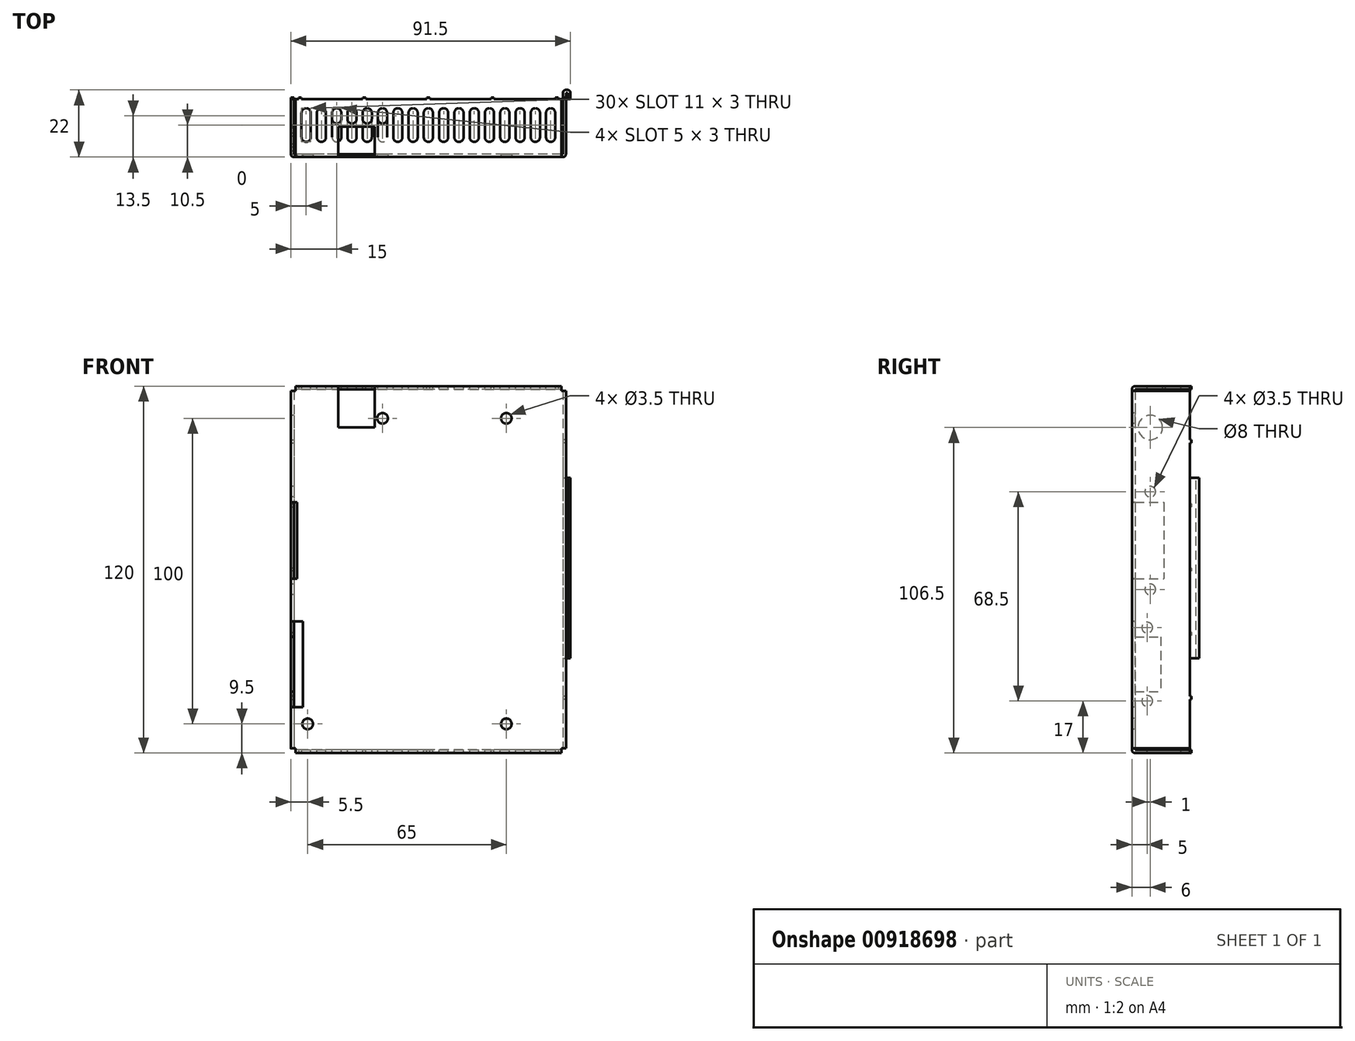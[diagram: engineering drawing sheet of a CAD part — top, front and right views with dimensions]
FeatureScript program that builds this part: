
annotation { "Feature Type Name" : "Feature", "Feature Type Description" : "" }
export const myFeature = defineFeature(function(context is Context, id is Id, definition is map)
    precondition{}
    {
        {
            var Q0;
            Q0=qCreatedBy(makeId("Front.planeOp"),FACE);
            var sketch = newSketch(context, id + "F0", { "sketchPlane" : qUnion([Q0])});
            skLineSegment(sketch, "E0.bottom", {"start": v(-45, 60) * mm, "end": v(45, 60) * mm});
            skLineSegment(sketch, "E0.top", {"start": v(-45, -60) * mm, "end": v(45, -60) * mm});
            skLineSegment(sketch, "E0.left", {"start": v(-45, 60) * mm, "end": v(-45, -60) * mm});
            skLineSegment(sketch, "E0.right", {"start": v(45, 60) * mm, "end": v(45, -60) * mm});
            skPoint(sketch, "E1", {"position": v(45, 0) * mm});
            skPoint(sketch, "E2", {"position": v(0, 60) * mm});
            skSolve(sketch);
        }
        {
            var Q0;
            Q0=qSketchRegion(id+"F0",true);
            extrude(context, id + "F1", {"entities" : qUnion([Q0]), "oppositeDirection" : true, "depth" : 1 * mm, "offsetDistance" : 25 * mm});
        }
        {
            var Q0;
            Q0=makeQuery(id+"F1.opExtrude","CAP_FACE",FACE,{"disambiguationData":[OSD([sQuery(id+"F0.wireOp",EDGE,"E0.bottom"),sQuery(id+"F0.wireOp",EDGE,"E0.top"),sQuery(id+"F0.wireOp",EDGE,"E0.left"),sQuery(id+"F0.wireOp",EDGE,"E0.right")])],"isStart":false});
            var sketch = newSketch(context, id + "F2", { "sketchPlane" : qUnion([Q0])});
            skLineSegment(sketch, "E3.bottom", {"start": v(-43.5, 60) * mm, "end": v(43.5, 60) * mm});
            skLineSegment(sketch, "E3.top", {"start": v(-43.5, 59) * mm, "end": v(43.5, 59) * mm});
            skLineSegment(sketch, "E3.left", {"start": v(-43.5, 60) * mm, "end": v(-43.5, 59) * mm});
            skLineSegment(sketch, "E3.right", {"start": v(43.5, 60) * mm, "end": v(43.5, 59) * mm});
            skLineSegment(sketch, "E4.bottom", {"start": v(-45, 58.5) * mm, "end": v(-44, 58.5) * mm});
            skLineSegment(sketch, "E4.top", {"start": v(-45, -58.5) * mm, "end": v(-44, -58.5) * mm});
            skLineSegment(sketch, "E4.left", {"start": v(-45, 58.5) * mm, "end": v(-45, -58.5) * mm});
            skLineSegment(sketch, "E4.right", {"start": v(-44, 58.5) * mm, "end": v(-44, -58.5) * mm});
            skLineSegment(sketch, "E5.bottom", {"start": v(45, 58.5) * mm, "end": v(44, 58.5) * mm});
            skLineSegment(sketch, "E5.top", {"start": v(45, -58.5) * mm, "end": v(44, -58.5) * mm});
            skLineSegment(sketch, "E5.left", {"start": v(45, 58.5) * mm, "end": v(45, -58.5) * mm});
            skLineSegment(sketch, "E5.right", {"start": v(44, 58.5) * mm, "end": v(44, -58.5) * mm});
            skLineSegment(sketch, "E6.bottom", {"start": v(-43.5, -59) * mm, "end": v(43.5, -59) * mm});
            skLineSegment(sketch, "E6.top", {"start": v(-43.5, -60) * mm, "end": v(43.5, -60) * mm});
            skLineSegment(sketch, "E6.left", {"start": v(-43.5, -59) * mm, "end": v(-43.5, -60) * mm});
            skLineSegment(sketch, "E6.right", {"start": v(43.5, -59) * mm, "end": v(43.5, -60) * mm});
            skSolve(sketch);
        }
        {
            var Q0;
            Q0=qSketchRegion(id+"F2",true);
            extrude(context, id + "F3", {"entities" : qUnion([Q0]), "operationType" : NewBodyOperationType.ADD, "depth" : 18 * mm, "offsetDistance" : 25 * mm});
        }
        {
            var Q0;
            Q0=makeQuery(id+"F1.opExtrude","CAP_FACE",FACE,{"disambiguationData":[OSD([sQuery(id+"F0.wireOp",EDGE,"E0.bottom"),sQuery(id+"F0.wireOp",EDGE,"E0.top"),sQuery(id+"F0.wireOp",EDGE,"E0.left"),sQuery(id+"F0.wireOp",EDGE,"E0.right")])],"isStart":false});
            var sketch = newSketch(context, id + "F4", { "sketchPlane" : qUnion([Q0])});
            skLineSegment(sketch, "E7.bottom", {"start": v(43.5, 60) * mm, "end": v(45, 60) * mm});
            skLineSegment(sketch, "E7.top", {"start": v(43.5, 58.5) * mm, "end": v(45, 58.5) * mm});
            skLineSegment(sketch, "E7.left", {"start": v(43.5, 60) * mm, "end": v(43.5, 58.5) * mm});
            skLineSegment(sketch, "E7.right", {"start": v(45, 60) * mm, "end": v(45, 58.5) * mm});
            skLineSegment(sketch, "E8.bottom", {"start": v(-45, 58.5) * mm, "end": v(-43.5, 58.5) * mm});
            skLineSegment(sketch, "E8.top", {"start": v(-45, 60) * mm, "end": v(-43.5, 60) * mm});
            skLineSegment(sketch, "E8.left", {"start": v(-45, 58.5) * mm, "end": v(-45, 60) * mm});
            skLineSegment(sketch, "E8.right", {"start": v(-43.5, 58.5) * mm, "end": v(-43.5, 60) * mm});
            skLineSegment(sketch, "E9.bottom", {"start": v(43.5, -60) * mm, "end": v(45, -60) * mm});
            skLineSegment(sketch, "E9.top", {"start": v(43.5, -58.5) * mm, "end": v(45, -58.5) * mm});
            skLineSegment(sketch, "E9.left", {"start": v(43.5, -60) * mm, "end": v(43.5, -58.5) * mm});
            skLineSegment(sketch, "E9.right", {"start": v(45, -60) * mm, "end": v(45, -58.5) * mm});
            skLineSegment(sketch, "E10.bottom", {"start": v(-45, -58.5) * mm, "end": v(-43.5, -58.5) * mm});
            skLineSegment(sketch, "E10.top", {"start": v(-45, -60) * mm, "end": v(-43.5, -60) * mm});
            skLineSegment(sketch, "E10.left", {"start": v(-45, -58.5) * mm, "end": v(-45, -60) * mm});
            skLineSegment(sketch, "E10.right", {"start": v(-43.5, -58.5) * mm, "end": v(-43.5, -60) * mm});
            skSolve(sketch);
        }
        {
            var Q0;
            Q0=qSketchRegion(id+"F4",true);
            extrude(context, id + "F5", {"entities" : qUnion([Q0]), "operationType" : NewBodyOperationType.REMOVE, "endBound" : BoundingType.THROUGH_ALL, "oppositeDirection" : true, "depth" : 25 * mm, "offsetDistance" : 25 * mm});
        }
        {
            var Q0;
            Q0=makeQuery(id+"F3.boolean.opBoolean","MERGE",FACE,{"derivedFrom":[makeQuery(id+"F1.opExtrude","SWEPT_FACE",FACE,{"disambiguationData":[OSD([sQuery(id+"F0.wireOp",EDGE,"E0.bottom")])]}),makeQuery(id+"F3.opExtrude","SWEPT_FACE",FACE,{"disambiguationData":[OSD([sQuery(id+"F2.wireOp",EDGE,"E3.bottom")])]})]});
            var sketch = newSketch(context, id + "F6", { "sketchPlane" : qUnion([Q0])});
            skLineSegment(sketch, "E11.left", {"start": v(1.5, 6.5) * mm, "end": v(1.5, 14.5) * mm});
            skLineSegment(sketch, "E11.right", {"start": v(-1.5, 6.5) * mm, "end": v(-1.5, 14.5) * mm});
            skArc(sketch, "E12", {"start": v(-1.5, 6.5) * mm, "mid": v(0, 5) * mm, "end": v(1.5, 6.5) * mm});
            skArc(sketch, "E13", {"start": v(1.5, 14.5) * mm, "mid": v(0, 16) * mm, "end": v(-1.5, 14.5) * mm});
            skPoint(sketch, "E14", {"position": v(0, 5) * mm});
            skPoint(sketch, "E15", {"position": v(0, 16) * mm});
            skLineSegment(sketch, "E16.left", {"start": v(-3.5, 6.5) * mm, "end": v(-3.5, 14.5) * mm});
            skLineSegment(sketch, "E16.right", {"start": v(-6.5, 6.5) * mm, "end": v(-6.5, 14.5) * mm});
            skArc(sketch, "E17", {"start": v(-6.5, 6.5) * mm, "mid": v(-5, 5) * mm, "end": v(-3.5, 6.5) * mm});
            skArc(sketch, "E18", {"start": v(-3.5, 14.5) * mm, "mid": v(-5, 16) * mm, "end": v(-6.5, 14.5) * mm});
            skPoint(sketch, "E19", {"position": v(-5, 5) * mm});
            skPoint(sketch, "E20", {"position": v(-5, 16) * mm});
            skLineSegment(sketch, "E21.left", {"start": v(-8.5, 6.5) * mm, "end": v(-8.5, 14.5) * mm});
            skLineSegment(sketch, "E21.right", {"start": v(-11.5, 6.5) * mm, "end": v(-11.5, 14.5) * mm});
            skArc(sketch, "E22", {"start": v(-11.5, 6.5) * mm, "mid": v(-10, 5) * mm, "end": v(-8.5, 6.5) * mm});
            skArc(sketch, "E23", {"start": v(-8.5, 14.5) * mm, "mid": v(-10, 16) * mm, "end": v(-11.5, 14.5) * mm});
            skPoint(sketch, "E24", {"position": v(-10, 5) * mm});
            skPoint(sketch, "E25", {"position": v(-10, 16) * mm});
            skLineSegment(sketch, "E26.left", {"start": v(-13.5, 12.5) * mm, "end": v(-13.5, 14.5) * mm});
            skLineSegment(sketch, "E26.right", {"start": v(-16.5, 12.5) * mm, "end": v(-16.5, 14.5) * mm});
            skArc(sketch, "E27", {"start": v(-16.5, 12.5) * mm, "mid": v(-15, 11) * mm, "end": v(-13.5, 12.5) * mm});
            skArc(sketch, "E28", {"start": v(-13.5, 14.5) * mm, "mid": v(-15, 16) * mm, "end": v(-16.5, 14.5) * mm});
            skPoint(sketch, "E29", {"position": v(-15, 11) * mm});
            skPoint(sketch, "E30", {"position": v(-15, 16) * mm});
            skLineSegment(sketch, "E31.left", {"start": v(11.5, 6.5) * mm, "end": v(11.5, 14.5) * mm});
            skLineSegment(sketch, "E31.right", {"start": v(8.5, 6.5) * mm, "end": v(8.5, 14.5) * mm});
            skArc(sketch, "E32", {"start": v(8.5, 6.5) * mm, "mid": v(10, 5) * mm, "end": v(11.5, 6.5) * mm});
            skArc(sketch, "E33", {"start": v(11.5, 14.5) * mm, "mid": v(10, 16) * mm, "end": v(8.5, 14.5) * mm});
            skPoint(sketch, "E34", {"position": v(10, 5) * mm});
            skPoint(sketch, "E35", {"position": v(10, 16) * mm});
            skLineSegment(sketch, "E36.left", {"start": v(6.5, 6.5) * mm, "end": v(6.5, 14.5) * mm});
            skLineSegment(sketch, "E36.right", {"start": v(3.5, 6.5) * mm, "end": v(3.5, 14.5) * mm});
            skArc(sketch, "E37", {"start": v(3.5, 6.5) * mm, "mid": v(5, 5) * mm, "end": v(6.5, 6.5) * mm});
            skArc(sketch, "E38", {"start": v(6.5, 14.5) * mm, "mid": v(5, 16) * mm, "end": v(3.5, 14.5) * mm});
            skPoint(sketch, "E39", {"position": v(5, 5) * mm});
            skPoint(sketch, "E40", {"position": v(5, 16) * mm});
            skLineSegment(sketch, "E41.left", {"start": v(16.5, 6.5) * mm, "end": v(16.5, 14.5) * mm});
            skLineSegment(sketch, "E41.right", {"start": v(13.5, 6.5) * mm, "end": v(13.5, 14.5) * mm});
            skArc(sketch, "E42", {"start": v(13.5, 6.5) * mm, "mid": v(15, 5) * mm, "end": v(16.5, 6.5) * mm});
            skArc(sketch, "E43", {"start": v(16.5, 14.5) * mm, "mid": v(15, 16) * mm, "end": v(13.5, 14.5) * mm});
            skPoint(sketch, "E44", {"position": v(15, 5) * mm});
            skPoint(sketch, "E45", {"position": v(15, 16) * mm});
            skLineSegment(sketch, "E46.left", {"start": v(-18.5, 12.5) * mm, "end": v(-18.5, 14.5) * mm});
            skLineSegment(sketch, "E46.right", {"start": v(-21.5, 12.5) * mm, "end": v(-21.5, 14.5) * mm});
            skArc(sketch, "E47", {"start": v(-21.5, 12.5) * mm, "mid": v(-20, 11) * mm, "end": v(-18.5, 12.5) * mm});
            skArc(sketch, "E48", {"start": v(-18.5, 14.5) * mm, "mid": v(-20, 16) * mm, "end": v(-21.5, 14.5) * mm});
            skPoint(sketch, "E49", {"position": v(-20, 11) * mm});
            skPoint(sketch, "E50", {"position": v(-20, 16) * mm});
            skLineSegment(sketch, "E51.left", {"start": v(-23.5, 12.5) * mm, "end": v(-23.5, 14.5) * mm});
            skLineSegment(sketch, "E51.right", {"start": v(-26.5, 12.5) * mm, "end": v(-26.5, 14.5) * mm});
            skArc(sketch, "E52", {"start": v(-26.5, 12.5) * mm, "mid": v(-25, 11) * mm, "end": v(-23.5, 12.5) * mm});
            skArc(sketch, "E53", {"start": v(-23.5, 14.5) * mm, "mid": v(-25, 16) * mm, "end": v(-26.5, 14.5) * mm});
            skPoint(sketch, "E54", {"position": v(-25, 5) * mm});
            skPoint(sketch, "E55", {"position": v(-25, 16) * mm});
            skLineSegment(sketch, "E56.left", {"start": v(-28.5, 12.5) * mm, "end": v(-28.5, 14.5) * mm});
            skLineSegment(sketch, "E56.right", {"start": v(-31.5, 12.5) * mm, "end": v(-31.5, 14.5) * mm});
            skArc(sketch, "E57", {"start": v(-31.5, 12.5) * mm, "mid": v(-30, 11) * mm, "end": v(-28.5, 12.5) * mm});
            skArc(sketch, "E58", {"start": v(-28.5, 14.5) * mm, "mid": v(-30, 16) * mm, "end": v(-31.5, 14.5) * mm});
            skPoint(sketch, "E59", {"position": v(-30, 11) * mm});
            skPoint(sketch, "E60", {"position": v(-30, 16) * mm});
            skLineSegment(sketch, "E61.left", {"start": v(-33.5, 6.5) * mm, "end": v(-33.5, 14.5) * mm});
            skLineSegment(sketch, "E61.right", {"start": v(-36.5, 6.5) * mm, "end": v(-36.5, 14.5) * mm});
            skArc(sketch, "E62", {"start": v(-36.5, 6.5) * mm, "mid": v(-35, 5) * mm, "end": v(-33.5, 6.5) * mm});
            skArc(sketch, "E63", {"start": v(-33.5, 14.5) * mm, "mid": v(-35, 16) * mm, "end": v(-36.5, 14.5) * mm});
            skPoint(sketch, "E64", {"position": v(-35, 5) * mm});
            skPoint(sketch, "E65", {"position": v(-35, 16) * mm});
            skLineSegment(sketch, "E66.left", {"start": v(36.5, 6.5) * mm, "end": v(36.5, 14.5) * mm});
            skLineSegment(sketch, "E66.right", {"start": v(33.5, 6.5) * mm, "end": v(33.5, 14.5) * mm});
            skArc(sketch, "E67", {"start": v(33.5, 6.5) * mm, "mid": v(35, 5) * mm, "end": v(36.5, 6.5) * mm});
            skArc(sketch, "E68", {"start": v(36.5, 14.5) * mm, "mid": v(35, 16) * mm, "end": v(33.5, 14.5) * mm});
            skPoint(sketch, "E69", {"position": v(35, 5) * mm});
            skPoint(sketch, "E70", {"position": v(35, 16) * mm});
            skLineSegment(sketch, "E71.left", {"start": v(31.5, 6.5) * mm, "end": v(31.5, 14.5) * mm});
            skLineSegment(sketch, "E71.right", {"start": v(28.5, 6.5) * mm, "end": v(28.5, 14.5) * mm});
            skArc(sketch, "E72", {"start": v(28.5, 6.5) * mm, "mid": v(30, 5) * mm, "end": v(31.5, 6.5) * mm});
            skArc(sketch, "E73", {"start": v(31.5, 14.5) * mm, "mid": v(30, 16) * mm, "end": v(28.5, 14.5) * mm});
            skPoint(sketch, "E74", {"position": v(30, 5) * mm});
            skPoint(sketch, "E75", {"position": v(30, 16) * mm});
            skLineSegment(sketch, "E76.left", {"start": v(26.5, 6.5) * mm, "end": v(26.5, 14.5) * mm});
            skLineSegment(sketch, "E76.right", {"start": v(23.5, 6.5) * mm, "end": v(23.5, 14.5) * mm});
            skArc(sketch, "E77", {"start": v(23.5, 6.5) * mm, "mid": v(25, 5) * mm, "end": v(26.5, 6.5) * mm});
            skArc(sketch, "E78", {"start": v(26.5, 14.5) * mm, "mid": v(25, 16) * mm, "end": v(23.5, 14.5) * mm});
            skPoint(sketch, "E79", {"position": v(25, 5) * mm});
            skPoint(sketch, "E80", {"position": v(25, 16) * mm});
            skLineSegment(sketch, "E81.left", {"start": v(21.5, 6.5) * mm, "end": v(21.5, 14.5) * mm});
            skLineSegment(sketch, "E81.right", {"start": v(18.5, 6.5) * mm, "end": v(18.5, 14.5) * mm});
            skArc(sketch, "E82", {"start": v(18.5, 6.5) * mm, "mid": v(20, 5) * mm, "end": v(21.5, 6.5) * mm});
            skArc(sketch, "E83", {"start": v(21.5, 14.5) * mm, "mid": v(20, 16) * mm, "end": v(18.5, 14.5) * mm});
            skPoint(sketch, "E84", {"position": v(20, 5) * mm});
            skPoint(sketch, "E85", {"position": v(20, 16) * mm});
            skLineSegment(sketch, "E86.left", {"start": v(-38.5, 6.5) * mm, "end": v(-38.5, 14.5) * mm});
            skLineSegment(sketch, "E86.right", {"start": v(-41.5, 6.5) * mm, "end": v(-41.5, 14.5) * mm});
            skArc(sketch, "E87", {"start": v(-41.5, 6.5) * mm, "mid": v(-40, 5) * mm, "end": v(-38.5, 6.5) * mm});
            skArc(sketch, "E88", {"start": v(-38.5, 14.5) * mm, "mid": v(-40, 16) * mm, "end": v(-41.5, 14.5) * mm});
            skPoint(sketch, "E89", {"position": v(-40, 5) * mm});
            skPoint(sketch, "E90", {"position": v(-40, 16) * mm});
            skLineSegment(sketch, "E91.left", {"start": v(41.5, 6.5) * mm, "end": v(41.5, 14.5) * mm});
            skLineSegment(sketch, "E91.right", {"start": v(38.5, 6.5) * mm, "end": v(38.5, 14.5) * mm});
            skArc(sketch, "E92", {"start": v(38.5, 6.5) * mm, "mid": v(40, 5) * mm, "end": v(41.5, 6.5) * mm});
            skArc(sketch, "E93", {"start": v(41.5, 14.5) * mm, "mid": v(40, 16) * mm, "end": v(38.5, 14.5) * mm});
            skPoint(sketch, "E94", {"position": v(40, 5) * mm});
            skPoint(sketch, "E95", {"position": v(40, 16) * mm});
            skSolve(sketch);
        }
        {
            var Q0;
            Q0=qSketchRegion(id+"F6",true);
            extrude(context, id + "F7", {"entities" : qUnion([Q0]), "operationType" : NewBodyOperationType.REMOVE, "endBound" : BoundingType.THROUGH_ALL, "oppositeDirection" : true, "depth" : 25 * mm, "offsetDistance" : 25 * mm});
        }
        {
            var Q0;
            Q0=makeQuery(id+"F3.opExtrude","CAP_FACE",FACE,{"disambiguationData":[OSD([sQuery(id+"F2.wireOp",EDGE,"E5.bottom"),sQuery(id+"F2.wireOp",EDGE,"E5.top"),sQuery(id+"F2.wireOp",EDGE,"E5.left"),sQuery(id+"F2.wireOp",EDGE,"E5.right")])],"isStart":false});
            var sketch = newSketch(context, id + "F8", { "sketchPlane" : qUnion([Q0])});
            skLineSegment(sketch, "E96.bottom", {"start": v(0.5, -60) * mm, "end": v(-0.5, -60) * mm});
            skLineSegment(sketch, "E96.top", {"start": v(0.5, -59) * mm, "end": v(-0.5, -59) * mm});
            skLineSegment(sketch, "E96.left", {"start": v(0.5, -60) * mm, "end": v(0.5, -59) * mm});
            skLineSegment(sketch, "E96.right", {"start": v(-0.5, -60) * mm, "end": v(-0.5, -59) * mm});
            skLineSegment(sketch, "E97.bottom", {"start": v(0.5, 59) * mm, "end": v(-0.5, 59) * mm});
            skLineSegment(sketch, "E97.top", {"start": v(0.5, 60) * mm, "end": v(-0.5, 60) * mm});
            skLineSegment(sketch, "E97.left", {"start": v(0.5, 59) * mm, "end": v(0.5, 60) * mm});
            skLineSegment(sketch, "E97.right", {"start": v(-0.5, 59) * mm, "end": v(-0.5, 60) * mm});
            skLineSegment(sketch, "E98.bottom", {"start": v(45, 20.5) * mm, "end": v(44, 20.5) * mm});
            skLineSegment(sketch, "E98.top", {"start": v(45, 21.5) * mm, "end": v(44, 21.5) * mm});
            skLineSegment(sketch, "E98.left", {"start": v(45, 20.5) * mm, "end": v(45, 21.5) * mm});
            skLineSegment(sketch, "E98.right", {"start": v(44, 20.5) * mm, "end": v(44, 21.5) * mm});
            skLineSegment(sketch, "E99.bottom", {"start": v(45, -21.5) * mm, "end": v(44, -21.5) * mm});
            skLineSegment(sketch, "E99.top", {"start": v(45, -20.5) * mm, "end": v(44, -20.5) * mm});
            skLineSegment(sketch, "E99.left", {"start": v(45, -21.5) * mm, "end": v(45, -20.5) * mm});
            skLineSegment(sketch, "E99.right", {"start": v(44, -21.5) * mm, "end": v(44, -20.5) * mm});
            skPoint(sketch, "E100", {"position": v(0, -59) * mm});
            skPoint(sketch, "E101", {"position": v(0, 59) * mm});
            skPoint(sketch, "E102", {"position": v(44, 21) * mm});
            skPoint(sketch, "E103", {"position": v(44, -21) * mm});
            skLineSegment(sketch, "E104.bottom", {"start": v(44, 0.5) * mm, "end": v(45, 0.5) * mm});
            skLineSegment(sketch, "E104.top", {"start": v(44, -0.5) * mm, "end": v(45, -0.5) * mm});
            skLineSegment(sketch, "E104.left", {"start": v(44, 0.5) * mm, "end": v(44, -0.5) * mm});
            skLineSegment(sketch, "E104.right", {"start": v(45, 0.5) * mm, "end": v(45, -0.5) * mm});
            skPoint(sketch, "E105", {"position": v(44, 0) * mm});
            skLineSegment(sketch, "E106.bottom", {"start": v(45, -42.5) * mm, "end": v(44, -42.5) * mm});
            skLineSegment(sketch, "E106.top", {"start": v(45, -41.5) * mm, "end": v(44, -41.5) * mm});
            skLineSegment(sketch, "E106.left", {"start": v(45, -42.5) * mm, "end": v(45, -41.5) * mm});
            skLineSegment(sketch, "E106.right", {"start": v(44, -42.5) * mm, "end": v(44, -41.5) * mm});
            skPoint(sketch, "E107", {"position": v(45, -42) * mm});
            skLineSegment(sketch, "E108.bottom", {"start": v(21.5, -60) * mm, "end": v(20.5, -60) * mm});
            skLineSegment(sketch, "E108.top", {"start": v(21.5, -59) * mm, "end": v(20.5, -59) * mm});
            skLineSegment(sketch, "E108.left", {"start": v(20.5, -60) * mm, "end": v(20.5, -59) * mm});
            skLineSegment(sketch, "E108.right", {"start": v(21.5, -60) * mm, "end": v(21.5, -59) * mm});
            skPoint(sketch, "E109", {"position": v(20.5, -59.5) * mm});
            skLineSegment(sketch, "E110.bottom", {"start": v(-20.5, 59) * mm, "end": v(-21.5, 59) * mm});
            skLineSegment(sketch, "E110.top", {"start": v(-20.5, 60) * mm, "end": v(-21.5, 60) * mm});
            skLineSegment(sketch, "E110.left", {"start": v(-21.5, 59) * mm, "end": v(-21.5, 60) * mm});
            skLineSegment(sketch, "E110.right", {"start": v(-20.5, 59) * mm, "end": v(-20.5, 60) * mm});
            skPoint(sketch, "E111", {"position": v(-21.5, 59.5) * mm});
            skLineSegment(sketch, "E112.bottom", {"start": v(21.5, 59) * mm, "end": v(20.5, 59) * mm});
            skLineSegment(sketch, "E112.top", {"start": v(21.5, 60) * mm, "end": v(20.5, 60) * mm});
            skLineSegment(sketch, "E112.left", {"start": v(20.5, 59) * mm, "end": v(20.5, 60) * mm});
            skLineSegment(sketch, "E112.right", {"start": v(21.5, 59) * mm, "end": v(21.5, 60) * mm});
            skPoint(sketch, "E113", {"position": v(20.5, 59.5) * mm});
            skLineSegment(sketch, "E114.bottom", {"start": v(41.5, 60) * mm, "end": v(42.5, 60) * mm});
            skLineSegment(sketch, "E114.top", {"start": v(41.5, 59) * mm, "end": v(42.5, 59) * mm});
            skLineSegment(sketch, "E114.left", {"start": v(41.5, 60) * mm, "end": v(41.5, 59) * mm});
            skLineSegment(sketch, "E114.right", {"start": v(42.5, 60) * mm, "end": v(42.5, 59) * mm});
            skLineSegment(sketch, "E115.bottom", {"start": v(-42.5, 60) * mm, "end": v(-41.5, 60) * mm});
            skLineSegment(sketch, "E115.top", {"start": v(-42.5, 59) * mm, "end": v(-41.5, 59) * mm});
            skLineSegment(sketch, "E115.left", {"start": v(-42.5, 60) * mm, "end": v(-42.5, 59) * mm});
            skLineSegment(sketch, "E115.right", {"start": v(-41.5, 60) * mm, "end": v(-41.5, 59) * mm});
            skLineSegment(sketch, "E116.bottom", {"start": v(41.5, -59) * mm, "end": v(42.5, -59) * mm});
            skLineSegment(sketch, "E116.top", {"start": v(41.5, -60) * mm, "end": v(42.5, -60) * mm});
            skLineSegment(sketch, "E116.left", {"start": v(41.5, -59) * mm, "end": v(41.5, -60) * mm});
            skLineSegment(sketch, "E116.right", {"start": v(42.5, -59) * mm, "end": v(42.5, -60) * mm});
            skLineSegment(sketch, "E117.bottom", {"start": v(-20.5, -60) * mm, "end": v(-21.5, -60) * mm});
            skLineSegment(sketch, "E117.top", {"start": v(-20.5, -59) * mm, "end": v(-21.5, -59) * mm});
            skLineSegment(sketch, "E117.left", {"start": v(-21.5, -60) * mm, "end": v(-21.5, -59) * mm});
            skLineSegment(sketch, "E117.right", {"start": v(-20.5, -60) * mm, "end": v(-20.5, -59) * mm});
            skPoint(sketch, "E118", {"position": v(-21.5, -59.5) * mm});
            skLineSegment(sketch, "E119.bottom", {"start": v(-42.5, -59) * mm, "end": v(-41.5, -59) * mm});
            skLineSegment(sketch, "E119.top", {"start": v(-42.5, -60) * mm, "end": v(-41.5, -60) * mm});
            skLineSegment(sketch, "E119.left", {"start": v(-42.5, -59) * mm, "end": v(-42.5, -60) * mm});
            skLineSegment(sketch, "E119.right", {"start": v(-41.5, -59) * mm, "end": v(-41.5, -60) * mm});
            skLineSegment(sketch, "E120.bottom", {"start": v(45, 42.5) * mm, "end": v(44, 42.5) * mm});
            skLineSegment(sketch, "E120.top", {"start": v(45, 41.5) * mm, "end": v(44, 41.5) * mm});
            skLineSegment(sketch, "E120.left", {"start": v(45, 42.5) * mm, "end": v(45, 41.5) * mm});
            skLineSegment(sketch, "E120.right", {"start": v(44, 42.5) * mm, "end": v(44, 41.5) * mm});
            skLineSegment(sketch, "E121.bottom", {"start": v(-45, -41.5) * mm, "end": v(-44, -41.5) * mm});
            skLineSegment(sketch, "E121.top", {"start": v(-45, -42.5) * mm, "end": v(-44, -42.5) * mm});
            skLineSegment(sketch, "E121.left", {"start": v(-45, -41.5) * mm, "end": v(-45, -42.5) * mm});
            skLineSegment(sketch, "E121.right", {"start": v(-44, -41.5) * mm, "end": v(-44, -42.5) * mm});
            skLineSegment(sketch, "E122.bottom", {"start": v(-45, 42.5) * mm, "end": v(-44, 42.5) * mm});
            skLineSegment(sketch, "E122.top", {"start": v(-45, 41.5) * mm, "end": v(-44, 41.5) * mm});
            skLineSegment(sketch, "E122.left", {"start": v(-45, 42.5) * mm, "end": v(-45, 41.5) * mm});
            skLineSegment(sketch, "E122.right", {"start": v(-44, 42.5) * mm, "end": v(-44, 41.5) * mm});
            skSolve(sketch);
        }
        {
            var Q0;
            Q0=qSketchRegion(id+"F8",true);
            extrude(context, id + "F9", {"entities" : qUnion([Q0]), "operationType" : NewBodyOperationType.ADD, "depth" : 0.5 * mm, "offsetDistance" : 25 * mm});
        }
        {
            var Q0;
            Q0=makeQuery(id+"F1.opExtrude","CAP_EDGE",EDGE,{"disambiguationData":[OSD([sQuery(id+"F0.wireOp",EDGE,"E0.left")])],"isStart":true});
            var Q1;
            Q1=makeQuery(id+"F1.opExtrude","CAP_EDGE",EDGE,{"disambiguationData":[OSD([sQuery(id+"F0.wireOp",EDGE,"E0.bottom")])],"isStart":true});
            var Q2;
            Q2=makeQuery(id+"F1.opExtrude","CAP_EDGE",EDGE,{"disambiguationData":[OSD([sQuery(id+"F0.wireOp",EDGE,"E0.right")])],"isStart":true});
            var Q3;
            Q3=makeQuery(id+"F1.opExtrude","CAP_EDGE",EDGE,{"disambiguationData":[OSD([sQuery(id+"F0.wireOp",EDGE,"E0.top")])],"isStart":true});
            fillet(context, id + "F10", {"entities" : qUnion([Q0, Q1, Q2, Q3]), "radius" : 1 * mm, "tangentPropagation" : true, "allowEdgeOverflow" : false});
        }
        {
            var Q0;
            Q0=makeQuery(id+"F9.boolean.opBoolean","MERGE",FACE,{"derivedFrom":[makeQuery(id+"F3.boolean.opBoolean","MERGE",FACE,{"derivedFrom":[makeQuery(id+"F1.opExtrude","SWEPT_FACE",FACE,{"disambiguationData":[OSD([sQuery(id+"F0.wireOp",EDGE,"E0.left")])]}),makeQuery(id+"F3.opExtrude","SWEPT_FACE",FACE,{"disambiguationData":[OSD([sQuery(id+"F2.wireOp",EDGE,"E5.left")])]})]}),makeQuery(id+"F9.opExtrude","SWEPT_FACE",FACE,{"disambiguationData":[OSD([sQuery(id+"F8.wireOp",EDGE,"E98.left")])]}),makeQuery(id+"F9.opExtrude","SWEPT_FACE",FACE,{"disambiguationData":[OSD([sQuery(id+"F8.wireOp",EDGE,"E99.left")])]}),makeQuery(id+"F9.opExtrude","SWEPT_FACE",FACE,{"disambiguationData":[OSD([sQuery(id+"F8.wireOp",EDGE,"E104.right")])]})]});
            var sketch = newSketch(context, id + "F11", { "sketchPlane" : qUnion([Q0])});
            skLineSegment(sketch, "E123.bottom", {"start": v(-0.5, -22) * mm, "end": v(-9.5, -22) * mm});
            skLineSegment(sketch, "E123.top", {"start": v(-0.5, -40) * mm, "end": v(-9.5, -40) * mm});
            skLineSegment(sketch, "E123.left", {"start": v(-0.5, -22) * mm, "end": v(-0.5, -40) * mm});
            skLineSegment(sketch, "E123.right", {"start": v(-9.5, -22) * mm, "end": v(-9.5, -40) * mm});
            skLineSegment(sketch, "E124.bottom", {"start": v(-1.5, 22) * mm, "end": v(-10.5, 22) * mm});
            skLineSegment(sketch, "E124.top", {"start": v(-1.5, -3) * mm, "end": v(-10.5, -3) * mm});
            skLineSegment(sketch, "E124.left", {"start": v(-1.5, 22) * mm, "end": v(-1.5, -3) * mm});
            skLineSegment(sketch, "E124.right", {"start": v(-10.5, 22) * mm, "end": v(-10.5, -3) * mm});
            skCircle(sketch, "E125", {"center": v(-6, 46.5) * mm, "radius": 4 * mm});
            skCircle(sketch, "E126", {"center": v(-6, 25.5) * mm, "radius": 1.75 * mm});
            skCircle(sketch, "E127", {"center": v(-6, -6.5) * mm, "radius": 1.75 * mm});
            skCircle(sketch, "E128", {"center": v(-5, -19) * mm, "radius": 1.75 * mm});
            skCircle(sketch, "E129", {"center": v(-5, -43) * mm, "radius": 1.75 * mm});
            skPoint(sketch, "E130", {"position": v(-6, 22) * mm});
            skPoint(sketch, "E131", {"position": v(-6, -3) * mm});
            skPoint(sketch, "E132", {"position": v(-5, -22) * mm});
            skPoint(sketch, "E133", {"position": v(-5, -40) * mm});
            skPoint(sketch, "E134", {"position": v(-9.5, -31) * mm});
            skPoint(sketch, "E135", {"position": v(-10.5, 9.5) * mm});
            skSolve(sketch);
        }
        {
            var Q0;
            Q0 = qSketchRegion(id + "F11", true);
            extrude(context, id + "F12", {"entities" : qUnion([Q0]), "operationType" : NewBodyOperationType.REMOVE, "oppositeDirection" : true, "depth" : 1 * mm, "offsetDistance" : 25 * mm});
        }
        {
            var Q0;
            Q0=makeQuery(id+"F9.boolean.opBoolean","MERGE",FACE,{"derivedFrom":[makeQuery(id+"F3.boolean.opBoolean","MERGE",FACE,{"derivedFrom":[makeQuery(id+"F1.opExtrude","SWEPT_FACE",FACE,{"disambiguationData":[OSD([sQuery(id+"F0.wireOp",EDGE,"E0.left")])]}),makeQuery(id+"F3.opExtrude","SWEPT_FACE",FACE,{"disambiguationData":[OSD([sQuery(id+"F2.wireOp",EDGE,"E5.left")])]})]}),makeQuery(id+"F9.opExtrude","SWEPT_FACE",FACE,{"disambiguationData":[OSD([sQuery(id+"F8.wireOp",EDGE,"E98.left")])]}),makeQuery(id+"F9.opExtrude","SWEPT_FACE",FACE,{"disambiguationData":[OSD([sQuery(id+"F8.wireOp",EDGE,"E99.left")])]}),makeQuery(id+"F9.opExtrude","SWEPT_FACE",FACE,{"disambiguationData":[OSD([sQuery(id+"F8.wireOp",EDGE,"E104.right")])]})]});
            var sketch = newSketch(context, id + "F13", { "sketchPlane" : qUnion([Q0])});
            skLineSegment(sketch, "E136.bottom", {"start": v(-1.5, 22) * mm, "end": v(0, 22) * mm});
            skLineSegment(sketch, "E136.top", {"start": v(-1.5, -3) * mm, "end": v(0, -3) * mm});
            skLineSegment(sketch, "E136.left", {"start": v(-1.5, 22) * mm, "end": v(-1.5, -3) * mm});
            skLineSegment(sketch, "E136.right", {"start": v(0, 22) * mm, "end": v(0, -3) * mm});
            skLineSegment(sketch, "E137.bottom", {"start": v(-1, -22) * mm, "end": v(0, -22) * mm});
            skLineSegment(sketch, "E137.top", {"start": v(-1, -40) * mm, "end": v(0, -40) * mm});
            skLineSegment(sketch, "E137.left", {"start": v(-1, -22) * mm, "end": v(-1, -40) * mm});
            skLineSegment(sketch, "E137.right", {"start": v(0, -22) * mm, "end": v(0, -40) * mm});
            skSolve(sketch);
        }
        {
            var Q0;
            Q0 = qSketchRegion(id + "F13", true);
            extrude(context, id + "F14", {"entities" : qUnion([Q0]), "operationType" : NewBodyOperationType.REMOVE, "oppositeDirection" : true, "depth" : 2 * mm, "offsetDistance" : 25 * mm});
        }
        {
            var Q0;
            Q0=makeQuery(id+"F1.opExtrude","CAP_FACE",FACE,{"disambiguationData":[OSD([sQuery(id+"F0.wireOp",EDGE,"E0.bottom"),sQuery(id+"F0.wireOp",EDGE,"E0.top"),sQuery(id+"F0.wireOp",EDGE,"E0.left"),sQuery(id+"F0.wireOp",EDGE,"E0.right")])],"isStart":true});
            var sketch = newSketch(context, id + "F15", { "sketchPlane" : qUnion([Q0])});
            skCircle(sketch, "E138", {"center": v(-39.5, -50.5) * mm, "radius": 1.75 * mm});
            skCircle(sketch, "E139", {"center": v(25.5, -50.5) * mm, "radius": 1.75 * mm});
            skCircle(sketch, "E140", {"center": v(25.5, 49.5) * mm, "radius": 1.75 * mm});
            skCircle(sketch, "E141", {"center": v(-15, 49.5) * mm, "radius": 1.75 * mm});
            skSolve(sketch);
        }
        {
            var Q0;
            Q0 = qSketchRegion(id + "F15", true);
            extrude(context, id + "F16", {"entities" : qUnion([Q0]), "operationType" : NewBodyOperationType.REMOVE, "endBound" : BoundingType.THROUGH_ALL, "oppositeDirection" : true, "depth" : 25 * mm, "offsetDistance" : 25 * mm});
        }
        {
            var Q0;
            Q0=makeQuery(id+"F9.boolean.opBoolean","MERGE",FACE,{"derivedFrom":[makeQuery(id+"F3.boolean.opBoolean","MERGE",FACE,{"derivedFrom":[makeQuery(id+"F1.opExtrude","SWEPT_FACE",FACE,{"disambiguationData":[OSD([sQuery(id+"F0.wireOp",EDGE,"E0.right")])]}),makeQuery(id+"F3.opExtrude","SWEPT_FACE",FACE,{"disambiguationData":[OSD([sQuery(id+"F2.wireOp",EDGE,"E4.left")])]})]}),makeQuery(id+"F9.opExtrude","SWEPT_FACE",FACE,{"disambiguationData":[OSD([sQuery(id+"F8.wireOp",EDGE,"tU1NsiTW-jNUZ-5MSe-Atkr-x9LIUrfDrN4e.right")])]}),makeQuery(id+"F9.opExtrude","SWEPT_FACE",FACE,{"disambiguationData":[OSD([sQuery(id+"F8.wireOp",EDGE,"PS19uuuy-x0m1-MYQr-Ssfi-21B9GRu6JML8.right")])]}),makeQuery(id+"F9.opExtrude","SWEPT_FACE",FACE,{"disambiguationData":[OSD([sQuery(id+"F8.wireOp",EDGE,"ryyqKuFn-6E0f-xOAN-ujbj-nhE9ARDO31tx.left")])]}),makeQuery(id+"F9.opExtrude","SWEPT_FACE",FACE,{"disambiguationData":[OSD([sQuery(id+"F8.wireOp",EDGE,"c2bce6ae-350b-4cfe-922f-e36637ce326e.right")])]})]});
            var sketch = newSketch(context, id + "F17", { "sketchPlane" : qUnion([Q0])});
            skLineSegment(sketch, "E142.bottom", {"start": v(19, 30) * mm, "end": v(22, 30) * mm});
            skLineSegment(sketch, "E142.top", {"start": v(19, -29) * mm, "end": v(22, -29) * mm});
            skLineSegment(sketch, "E142.left", {"start": v(19, 30) * mm, "end": v(19, -29) * mm});
            skLineSegment(sketch, "E142.right", {"start": v(22, 30) * mm, "end": v(22, -29) * mm});
            skSolve(sketch);
        }
        {
            var Q0;
            Q0 = qSketchRegion(id + "F17", true);
            extrude(context, id + "F18", {"entities" : qUnion([Q0]), "operationType" : NewBodyOperationType.ADD, "oppositeDirection" : true, "depth" : 1 * mm, "offsetDistance" : 25 * mm});
        }
        {
            var Q0;
            Q0=makeQuery(id+"F1.opExtrude","CAP_FACE",FACE,{"disambiguationData":[OSD([sQuery(id+"F0.wireOp",EDGE,"E0.bottom"),sQuery(id+"F0.wireOp",EDGE,"E0.top"),sQuery(id+"F0.wireOp",EDGE,"E0.left"),sQuery(id+"F0.wireOp",EDGE,"E0.right")])],"isStart":true});
            var sketch = newSketch(context, id + "F19", { "sketchPlane" : qUnion([Q0])});
            skLineSegment(sketch, "E143.top", {"start": v(-29.5, 46.5) * mm, "end": v(-17.5, 46.5) * mm});
            skLineSegment(sketch, "E143.left", {"start": v(-29.5, 60) * mm, "end": v(-29.5, 46.5) * mm});
            skPoint(sketch, "E144", {"position": v(-15, 49.5) * mm});
            skPoint(sketch, "E145", {"position": v(-23.5, 46.5) * mm});
            skLineSegment(sketch, "E146", {"start": v(-29.5, 60) * mm, "end": v(-17.5, 60) * mm});
            skLineSegment(sketch, "E147", {"start": v(-17.5, 60) * mm, "end": v(-17.5, 46.5) * mm});
            skSolve(sketch);
        }
        {
            var Q0;
            Q0 = qSketchRegion(id + "F19", true);
            extrude(context, id + "F20", {"entities" : qUnion([Q0]), "operationType" : NewBodyOperationType.REMOVE, "oppositeDirection" : true, "depth" : 10 * mm, "offsetDistance" : 25 * mm});
        }
        {
            var Q0;
            Q0=makeQuery(id+"F1.opExtrude","CAP_FACE",FACE,{"disambiguationData":[OSD([sQuery(id+"F0.wireOp",EDGE,"E0.bottom"),sQuery(id+"F0.wireOp",EDGE,"E0.top"),sQuery(id+"F0.wireOp",EDGE,"E0.left"),sQuery(id+"F0.wireOp",EDGE,"E0.right")])],"isStart":true});
            var sketch = newSketch(context, id + "F21", { "sketchPlane" : qUnion([Q0])});
            skLineSegment(sketch, "E148.bottom", {"start": v(-41, -45) * mm, "end": v(-45, -45) * mm});
            skLineSegment(sketch, "E148.top", {"start": v(-41, -17) * mm, "end": v(-45, -17) * mm});
            skLineSegment(sketch, "E148.left", {"start": v(-41, -45) * mm, "end": v(-41, -17) * mm});
            skLineSegment(sketch, "E148.right", {"start": v(-45, -45) * mm, "end": v(-45, -17) * mm});
            skPoint(sketch, "E149", {"position": v(-45, -31) * mm});
            skSolve(sketch);
        }
        {
            var Q0;
            Q0 = qSketchRegion(id + "F21", true);
            extrude(context, id + "F22", {"entities" : qUnion([Q0]), "operationType" : NewBodyOperationType.REMOVE, "oppositeDirection" : true, "depth" : 1 * mm, "offsetDistance" : 25 * mm});
        }
        {
            var Q0;
            Q0=makeQuery(id+"F18.boolean.opBoolean","MERGE",FACE,{"derivedFrom":[makeQuery(id+"F9.boolean.opBoolean","MERGE",FACE,{"derivedFrom":[makeQuery(id+"F3.boolean.opBoolean","MERGE",FACE,{"derivedFrom":[makeQuery(id+"F1.opExtrude","SWEPT_FACE",FACE,{"disambiguationData":[OSD([sQuery(id+"F0.wireOp",EDGE,"E0.right")])]}),makeQuery(id+"F3.opExtrude","SWEPT_FACE",FACE,{"disambiguationData":[OSD([sQuery(id+"F2.wireOp",EDGE,"E4.left")])]})]}),makeQuery(id+"F9.opExtrude","SWEPT_FACE",FACE,{"disambiguationData":[OSD([sQuery(id+"F8.wireOp",EDGE,"E121.left")])]}),makeQuery(id+"F9.opExtrude","SWEPT_FACE",FACE,{"disambiguationData":[OSD([sQuery(id+"F8.wireOp",EDGE,"E122.left")])]})]}),makeQuery(id+"F18.opExtrude","CAP_FACE",FACE,{"disambiguationData":[OSD([sQuery(id+"F17.wireOp",EDGE,"E142.bottom"),sQuery(id+"F17.wireOp",EDGE,"E142.top"),sQuery(id+"F17.wireOp",EDGE,"E142.left"),sQuery(id+"F17.wireOp",EDGE,"E142.right")])],"isStart":true})]});
            var sketch = newSketch(context, id + "F23", { "sketchPlane" : qUnion([Q0])});
            skLineSegment(sketch, "E150.bottom", {"start": v(22, -29) * mm, "end": v(21, -29) * mm});
            skLineSegment(sketch, "E150.top", {"start": v(22, 30) * mm, "end": v(21, 30) * mm});
            skLineSegment(sketch, "E150.left", {"start": v(22, -29) * mm, "end": v(22, 30) * mm});
            skLineSegment(sketch, "E150.right", {"start": v(21, -29) * mm, "end": v(21, 30) * mm});
            skSolve(sketch);
        }
        {
            var Q0;
            Q0 = qSketchRegion(id + "F23", true);
            extrude(context, id + "F24", {"entities" : qUnion([Q0]), "operationType" : NewBodyOperationType.ADD, "depth" : 0.5 * mm, "offsetDistance" : 25 * mm});
        }
        {
            var Q0;
            Q0=makeQuery(id+"F24.opExtrude","CAP_FACE",FACE,{"disambiguationData":[OSD([sQuery(id+"F23.wireOp",EDGE,"E150.bottom"),sQuery(id+"F23.wireOp",EDGE,"E150.top"),sQuery(id+"F23.wireOp",EDGE,"E150.left"),sQuery(id+"F23.wireOp",EDGE,"E150.right")])],"isStart":false});
            var sketch = newSketch(context, id + "F25", { "sketchPlane" : qUnion([Q0])});
            skLineSegment(sketch, "E151.bottom", {"start": v(22, 30) * mm, "end": v(19, 30) * mm});
            skLineSegment(sketch, "E151.top", {"start": v(22, -29) * mm, "end": v(19, -29) * mm});
            skLineSegment(sketch, "E151.left", {"start": v(22, 30) * mm, "end": v(22, -29) * mm});
            skLineSegment(sketch, "E151.right", {"start": v(19, 30) * mm, "end": v(19, -29) * mm});
            skSolve(sketch);
        }
        {
            var Q0;
            Q0 = qSketchRegion(id + "F25", true);
            extrude(context, id + "F26", {"entities" : qUnion([Q0]), "operationType" : NewBodyOperationType.ADD, "depth" : 1 * mm, "offsetDistance" : 25 * mm});
        }
        {
            var Q0;
            Q0=makeQuery(id+"F26.opExtrude","CAP_EDGE",EDGE,{"disambiguationData":[OSD([sQuery(id+"F25.wireOp",EDGE,"E151.left")])],"isStart":false});
            var Q1;
            Q1=makeQuery(id+"F18.opExtrude","CAP_EDGE",EDGE,{"disambiguationData":[OSD([sQuery(id+"F17.wireOp",EDGE,"E142.right")])],"isStart":false});
            fillet(context, id + "F27", {"entities" : qUnion([Q0, Q1]), "radius" : 1 * mm, "tangentPropagation" : true, "allowEdgeOverflow" : false});
        }
        {
            var Q0;
            Q0=makeQuery(id+"F9.boolean.opBoolean","MERGE",FACE,{"derivedFrom":[makeQuery(id+"F3.boolean.opBoolean","MERGE",FACE,{"derivedFrom":[makeQuery(id+"F1.opExtrude","SWEPT_FACE",FACE,{"disambiguationData":[OSD([sQuery(id+"F0.wireOp",EDGE,"E0.top")])]}),makeQuery(id+"F3.opExtrude","SWEPT_FACE",FACE,{"disambiguationData":[OSD([sQuery(id+"F2.wireOp",EDGE,"E6.top")])]})]}),makeQuery(id+"F9.opExtrude","SWEPT_FACE",FACE,{"disambiguationData":[OSD([sQuery(id+"F8.wireOp",EDGE,"E96.bottom")])]}),makeQuery(id+"F9.opExtrude","SWEPT_FACE",FACE,{"disambiguationData":[OSD([sQuery(id+"F8.wireOp",EDGE,"E108.bottom")])]}),makeQuery(id+"F9.opExtrude","SWEPT_FACE",FACE,{"disambiguationData":[OSD([sQuery(id+"F8.wireOp",EDGE,"E116.top")])]}),makeQuery(id+"F9.opExtrude","SWEPT_FACE",FACE,{"disambiguationData":[OSD([sQuery(id+"F8.wireOp",EDGE,"E117.bottom")])]}),makeQuery(id+"F9.opExtrude","SWEPT_FACE",FACE,{"disambiguationData":[OSD([sQuery(id+"F8.wireOp",EDGE,"E119.top")])]})]});
            var sketch = newSketch(context, id + "F28", { "sketchPlane" : qUnion([Q0])});
            skArc(sketch, "E152", {"start": v(-28.5, -6.5) * mm, "mid": v(-30, -5) * mm, "end": v(-31.5, -6.5) * mm});
            skLineSegment(sketch, "E153", {"start": v(-31.5, -12.5) * mm, "end": v(-31.5, -6.5) * mm});
            skLineSegment(sketch, "E154", {"start": v(-28.5, -12.5) * mm, "end": v(-28.5, -6.5) * mm});
            skLineSegment(sketch, "E155", {"start": v(-31.5, -12.5) * mm, "end": v(-28.5, -12.5) * mm});
            skArc(sketch, "E156", {"start": v(-23.5, -6.5) * mm, "mid": v(-25, -5) * mm, "end": v(-26.5, -6.5) * mm});
            skLineSegment(sketch, "E157", {"start": v(-26.5, -12.5) * mm, "end": v(-26.5, -6.5) * mm});
            skLineSegment(sketch, "E158", {"start": v(-23.5, -12.5) * mm, "end": v(-23.5, -6.5) * mm});
            skLineSegment(sketch, "E159", {"start": v(-26.5, -12.5) * mm, "end": v(-23.5, -12.5) * mm});
            skArc(sketch, "E160", {"start": v(-18.5, -6.5) * mm, "mid": v(-20, -5) * mm, "end": v(-21.5, -6.5) * mm});
            skLineSegment(sketch, "E161", {"start": v(-21.5, -12.5) * mm, "end": v(-21.5, -6.5) * mm});
            skLineSegment(sketch, "E162", {"start": v(-18.5, -12.5) * mm, "end": v(-18.5, -6.5) * mm});
            skLineSegment(sketch, "E163", {"start": v(-21.5, -12.5) * mm, "end": v(-18.5, -12.5) * mm});
            skArc(sketch, "E164", {"start": v(-13.5, -6.5) * mm, "mid": v(-15, -5) * mm, "end": v(-16.5, -6.5) * mm});
            skLineSegment(sketch, "E165", {"start": v(-16.5, -12.5) * mm, "end": v(-16.5, -6.5) * mm});
            skLineSegment(sketch, "E166", {"start": v(-13.5, -12.5) * mm, "end": v(-13.5, -6.5) * mm});
            skLineSegment(sketch, "E167", {"start": v(-16.5, -12.5) * mm, "end": v(-13.5, -12.5) * mm});
            skSolve(sketch);
        }
        {
            var Q0;
            Q0 = qSketchRegion(id + "F28", true);
            extrude(context, id + "F29", {"entities" : qUnion([Q0]), "operationType" : NewBodyOperationType.REMOVE, "oppositeDirection" : true, "depth" : 1 * mm, "offsetDistance" : 25 * mm});
        }
    });
